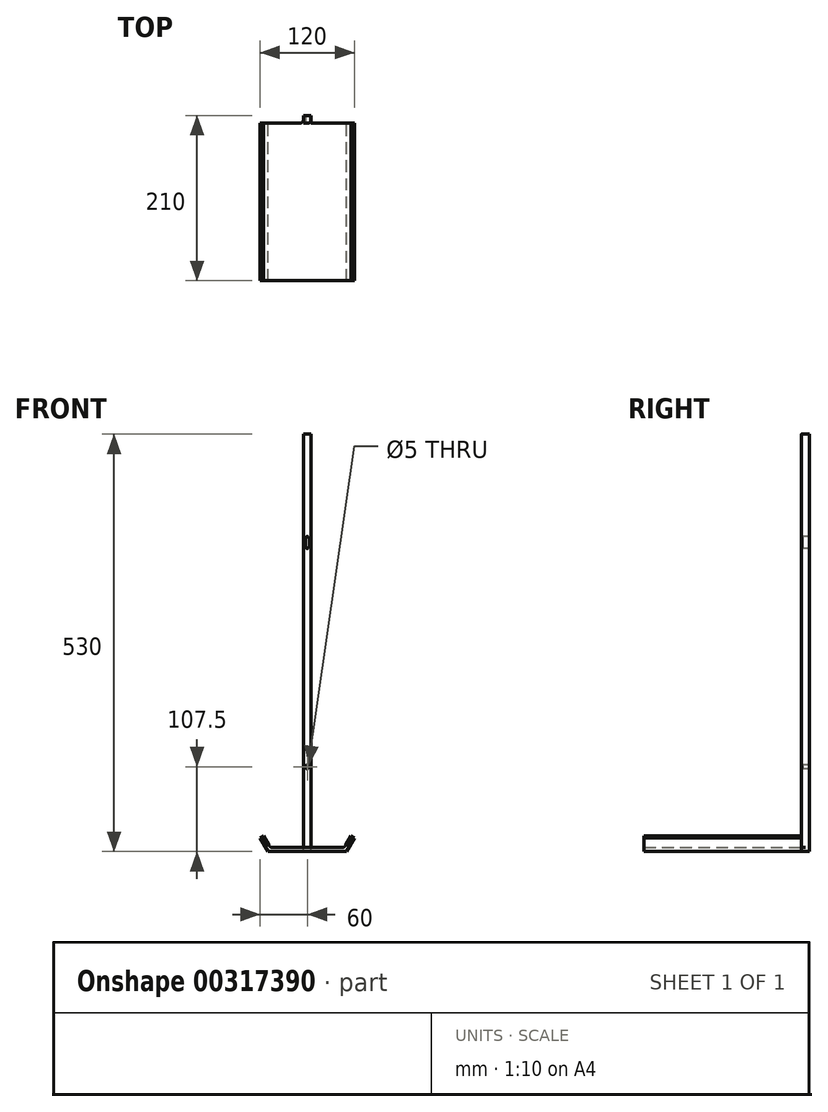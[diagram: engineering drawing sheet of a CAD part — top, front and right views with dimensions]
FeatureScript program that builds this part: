
annotation { "Feature Type Name" : "Feature", "Feature Type Description" : "" }
export const myFeature = defineFeature(function(context is Context, id is Id, definition is map)
    precondition{}
    {
        {
            var Q0;
            Q0=qCreatedBy(makeId("Front.planeOp"),FACE);
            var sketch = newSketch(context, id + "F0", { "sketchPlane" : qUnion([Q0])});
            skLineSegment(sketch, "E0", {"start": v(-50, 0) * mm, "end": v(0, 0) * mm});
            skLineSegment(sketch, "E1", {"start": v(0, 0) * mm, "end": v(50, 0) * mm});
            skLineSegment(sketch, "E2", {"start": v(50, 0) * mm, "end": v(60, 17.32) * mm});
            skLineSegment(sketch, "E3", {"start": v(-50, 0) * mm, "end": v(-60, 17.32) * mm});
            skLineSegment(sketch, "E4", {"start": v(-60, 17.32) * mm, "end": v(60, 17.32) * mm, "construction": true});
            skLineSegment(sketch, "E5.0", {"start": v(-47.11, 5) * mm, "end": v(-55.67, 19.82) * mm});
            skLineSegment(sketch, "E5.1", {"start": v(-47.11, 5) * mm, "end": v(0, 5) * mm});
            skLineSegment(sketch, "E5.2", {"start": v(0, 5) * mm, "end": v(47.11, 5) * mm});
            skLineSegment(sketch, "E5.3", {"start": v(47.11, 5) * mm, "end": v(55.67, 19.82) * mm});
            skLineSegment(sketch, "E6", {"start": v(-55.67, 19.82) * mm, "end": v(-60, 17.32) * mm});
            skLineSegment(sketch, "E7", {"start": v(55.67, 19.82) * mm, "end": v(60, 17.32) * mm});
            skSolve(sketch);
        }
        {
            var Q0;
            Q0 = qSketchRegion(id + "F0", true);
            extrude(context, id + "F1", {"entities" : qUnion([Q0]), "depth" : 200 * mm});
        }
        {
            var Q0;
            Q0=qCreatedBy(makeId("Front.planeOp"),FACE);
            var sketch = newSketch(context, id + "F2", { "sketchPlane" : qUnion([Q0])});
            skLineSegment(sketch, "E8.bottom", {"start": v(5, 0) * mm, "end": v(-5, 0) * mm});
            skLineSegment(sketch, "E8.top", {"start": v(5, 530) * mm, "end": v(-5, 530) * mm});
            skLineSegment(sketch, "E8.left", {"start": v(5, 0) * mm, "end": v(5, 530) * mm});
            skLineSegment(sketch, "E8.right", {"start": v(-5, 0) * mm, "end": v(-5, 530) * mm});
            skLineSegment(sketch, "E9", {"start": v(0, 0) * mm, "end": v(0, 530) * mm, "construction": true});
            skCircle(sketch, "E10", {"center": v(0, 107.5) * mm, "radius": 2.5 * mm});
            skCircle(sketch, "E11", {"center": v(0, 397.5) * mm, "radius": 2.5 * mm});
            skCircle(sketch, "E12", {"center": v(0, 387.5) * mm, "radius": 2.5 * mm});
            skLineSegment(sketch, "E13", {"start": v(-2.5, 397.5) * mm, "end": v(-2.5, 387.5) * mm});
            skLineSegment(sketch, "E14", {"start": v(2.5, 397.5) * mm, "end": v(2.5, 387.5) * mm});
            skSolve(sketch);
        }
        {
            var Q0;
            Q0 = qSketchRegion(id + "F2", true);
            extrude(context, id + "F3", {"entities" : qUnion([Q0]), "operationType" : NewBodyOperationType.ADD, "oppositeDirection" : true, "depth" : 10 * mm});
        }
        {
            var Q0;
            Q0=makeQuery(id+"F1.opExtrude","SWEPT_EDGE",EDGE,{"disambiguationData":[OSD([sQuery(id+"F0.wireOp",EDGE,"E5.2"),sQuery(id+"F0.wireOp",EDGE,"E5.3")])]});
            var Q1;
            Q1=makeQuery(id+"F1.opExtrude","SWEPT_EDGE",EDGE,{"disambiguationData":[OSD([sQuery(id+"F0.wireOp",EDGE,"E5.0"),sQuery(id+"F0.wireOp",EDGE,"E5.1")])]});
            var Q2;
            {var subQ0=sQuery(id+"F2.wireOp",EDGE,"E8.left");Q2=makeQuery(id+"F3.boolean.opBoolean","SPLIT",EDGE,{"disambiguationData":[topologyDisambiguationEdgeConnected([makeQuery(id+"F1.opExtrude","CAP_FACE",FACE,{"disambiguationData":[OSD([sQuery(id+"F0.wireOp",EDGE,"E0"),sQuery(id+"F0.wireOp",EDGE,"E1"),sQuery(id+"F0.wireOp",EDGE,"E2"),sQuery(id+"F0.wireOp",EDGE,"E3"),sQuery(id+"F0.wireOp",EDGE,"E5.0"),sQuery(id+"F0.wireOp",EDGE,"E5.1"),sQuery(id+"F0.wireOp",EDGE,"E5.2"),sQuery(id+"F0.wireOp",EDGE,"E5.3"),sQuery(id+"F0.wireOp",EDGE,"E6"),sQuery(id+"F0.wireOp",EDGE,"E7")])],"isStart":true})])],"derivedFrom":makeQuery(id+"F3.opExtrude","CAP_EDGE",EDGE,{"disambiguationData":[OSD([subQ0])],"isStart":true})});}
            var Q3;
            {var subQ0=sQuery(id+"F2.wireOp",EDGE,"E8.right");Q3=makeQuery(id+"F3.boolean.opBoolean","SPLIT",EDGE,{"disambiguationData":[topologyDisambiguationEdgeConnected([makeQuery(id+"F1.opExtrude","CAP_FACE",FACE,{"disambiguationData":[OSD([sQuery(id+"F0.wireOp",EDGE,"E0"),sQuery(id+"F0.wireOp",EDGE,"E1"),sQuery(id+"F0.wireOp",EDGE,"E2"),sQuery(id+"F0.wireOp",EDGE,"E3"),sQuery(id+"F0.wireOp",EDGE,"E5.0"),sQuery(id+"F0.wireOp",EDGE,"E5.1"),sQuery(id+"F0.wireOp",EDGE,"E5.2"),sQuery(id+"F0.wireOp",EDGE,"E5.3"),sQuery(id+"F0.wireOp",EDGE,"E6"),sQuery(id+"F0.wireOp",EDGE,"E7")])],"isStart":true})])],"derivedFrom":makeQuery(id+"F3.opExtrude","CAP_EDGE",EDGE,{"disambiguationData":[OSD([subQ0])],"isStart":true})});}
            fillet(context, id + "F4", {"entities" : qUnion([Q0, Q1, Q2, Q3]), "radius" : 5 * mm, "tangentPropagation" : true, "allowEdgeOverflow" : false});
        }
    });
